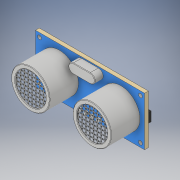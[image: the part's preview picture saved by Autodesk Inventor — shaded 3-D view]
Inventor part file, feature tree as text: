
AUTODESK INVENTOR PART (.ipt)
format: ipt  version: 2019 (Build 230136000, 136)  size: 341,504 bytes
history: native  units: mm
features: extrude x9, sketch x9, projected_geometry x6, chamfer x5, other x1, fillet x1
ambient origin geometry x8: Origin, YZ Plane, XZ Plane, XY Plane, X Axis, Y Axis, Z Axis, Center Point
bodies: Body1 (feature_tree)
feature tree (31):
  other  "Твердое тело1"
  extrude  "Выдавливание1"  Depth=45.4mm
  extrude  "Выдавливание2"  Depth=20.4mm
  extrude  "Выдавливание3"  Depth=42.0mm
  chamfer  "Фаска1"  Distance=17.0mm
  extrude  "Выдавливание4"  Depth=1.6mm
  extrude  "Выдавливание5"  Depth=1.6mm TaperAngle=0.0deg
  fillet  "Сопряжение1"  Radius=16.0mm
  extrude  "Выдавливание7"  Depth=25.6mm
  extrude  "Выдавливание8"  Depth=12.0mm TaperAngle=0.0deg
  chamfer  "Фаска2"  Distance=1.6mm
  extrude  "Выдавливание9"  Depth=0.4mm TaperAngle=0.0deg
  chamfer  "Фаска3"  Distance=2.0mm Angle=45.0deg
  extrude  "Выдавливание10"  Depth=7.0mm
  chamfer  "Фаска4"  Distance=2.0mm
  chamfer  "Фаска5"  Distance=2.5mm
  sketch  "Эскиз1"
  sketch  "Эскиз2"
  sketch  "Эскиз3"
  projected_geometry  "Спроецированная петля1"
  projected_geometry  "Спроецированная петля2"
  sketch  "Эскиз4"
  sketch  "Эскиз5"
  sketch  "Эскиз7"
  sketch  "Эскиз8"
  projected_geometry  "Спроецированная петля3"
  sketch  "Эскиз9"
  projected_geometry  "Спроецированная петля4"
  projected_geometry  "Спроецированная петля5"
  projected_geometry  "Спроецированная петля6"
  sketch  "Эскиз10"
